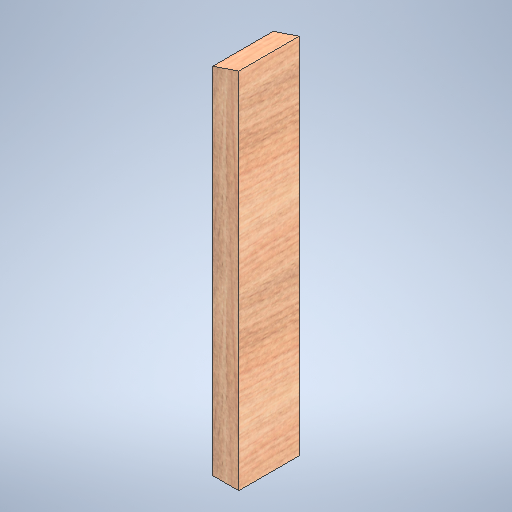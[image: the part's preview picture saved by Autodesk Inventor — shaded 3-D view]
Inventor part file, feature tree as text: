
AUTODESK INVENTOR PART (.ipt)
format: ipt  version: 2025.1 (Build 291241020, 241B)  size: 357,376 bytes
history: native  units: in
note: dims shown in document units (in); Inventor stores cm internally (conversion verified against a paired STEP export)
features: extrude x1, sketch x1
ambient origin geometry x8: Origin, YZ Plane, XZ Plane, XY Plane, X Axis, Y Axis, Z Axis, Center Point
bodies: Solid1 (feature_tree)
feature tree (2):
  extrude  "Extrusion1"  Depth=3.5in TaperAngle=0.0deg
  sketch  "Sketch1"  dims[d2=1.5in d3=3.5in d4=0.0in d5=20.562in d6=21.063in]
